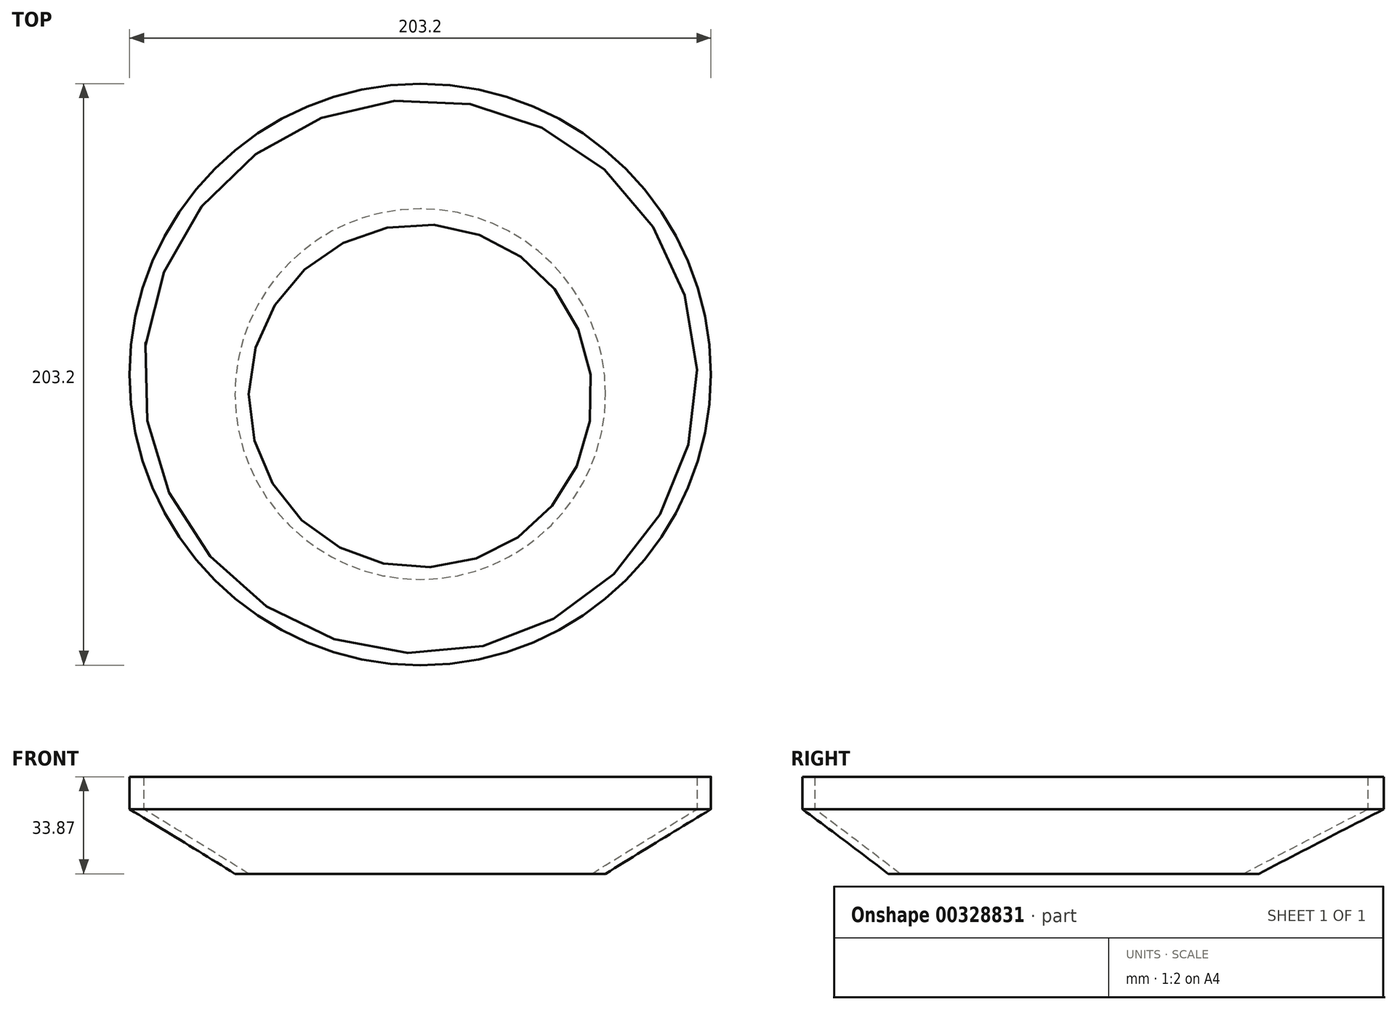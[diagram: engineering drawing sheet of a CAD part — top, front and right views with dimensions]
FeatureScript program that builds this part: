
annotation { "Feature Type Name" : "Feature", "Feature Type Description" : "" }
export const myFeature = defineFeature(function(context is Context, id is Id, definition is map)
    precondition{}
    {
        {
            var Q0;
            Q0=qCreatedBy(makeId("Top.planeOp"),FACE);
            var sketch = newSketch(context, id + "F0", { "sketchPlane" : qUnion([Q0])});
            skCircle(sketch, "E0", {"center": v(0, 0) * mm, "radius": 64.77 * mm});
            skSolve(sketch);
        }
        {
            var Q0;
            Q0=qCreatedBy(makeId("Top.planeOp"),FACE);
            cPlane(context, id + "F1", {"entities" : qUnion([Q0]), "cplaneType" : CPlaneType.OFFSET, "offset" : 22.58 * mm, "width" : 152.4 * mm, "height" : 152.4 * mm});
        }
        {
            var Q0;
            Q0=qCreatedBy(id+"F1.planeOp",FACE);
            var sketch = newSketch(context, id + "F2", { "sketchPlane" : qUnion([Q0])});
            skCircle(sketch, "E1", {"center": v(0, 6.87) * mm, "radius": 101.6 * mm});
            skSolve(sketch);
        }
        {
            var Q0;
            Q0=makeQuery(id+"F0.imprint","IMPRINT",FACE,{"disambiguationData":[TD([[makeQuery(id+"F0.imprint","IMPRINT",EDGE,{"derivedFrom":sQuery(id+"F0.wireOp",EDGE,"E0")}),1.0]])]});
            var Q1;
            Q1=makeQuery(id+"F2.imprint","IMPRINT",FACE,{"disambiguationData":[TD([[makeQuery(id+"F2.imprint","IMPRINT",EDGE,{"derivedFrom":sQuery(id+"F2.wireOp",EDGE,"E1")}),1.0]])]});
            loft(context, id + "F3", {"sheetProfilesArray" : [{ "sheetProfileEntities" : qUnion([Q0]) }, { "sheetProfileEntities" : qUnion([Q1]) }]});
        }
        {
            var Q0;
            Q0=makeQuery(id+"F3.opLoft","CAP_FACE",FACE,{"disambiguationData":[OSD([makeQuery(id+"F2.imprint","IMPRINT",FACE,{"disambiguationData":[TD([[makeQuery(id+"F2.imprint","IMPRINT",EDGE,{"derivedFrom":sQuery(id+"F2.wireOp",EDGE,"E1")}),1.0]])]})])],"isStart":true});
            var Q1;
            Q1=makeQuery(id+"F3.opLoft","CAP_FACE",FACE,{"disambiguationData":[OSD([makeQuery(id+"F0.imprint","IMPRINT",FACE,{"disambiguationData":[TD([[makeQuery(id+"F0.imprint","IMPRINT",EDGE,{"derivedFrom":sQuery(id+"F0.wireOp",EDGE,"E0")}),1.0]])]})])],"isStart":true});
            shell(context, id + "F4", {"entities" : qUnion([Q0, Q1]), "thickness" : 2.54 * mm});
        }
        {
            var Q0;
            Q0=makeQuery(id+"F3.opLoft","CAP_FACE",FACE,{"disambiguationData":[OSD([makeQuery(id+"F2.imprint","IMPRINT",FACE,{"disambiguationData":[TD([[makeQuery(id+"F2.imprint","IMPRINT",EDGE,{"derivedFrom":sQuery(id+"F2.wireOp",EDGE,"E1")}),1.0]])]})])],"isStart":true});
            extrude(context, id + "F5", {"entities" : qUnion([Q0]), "operationType" : NewBodyOperationType.ADD, "depth" : 11.29 * mm});
        }
    });
